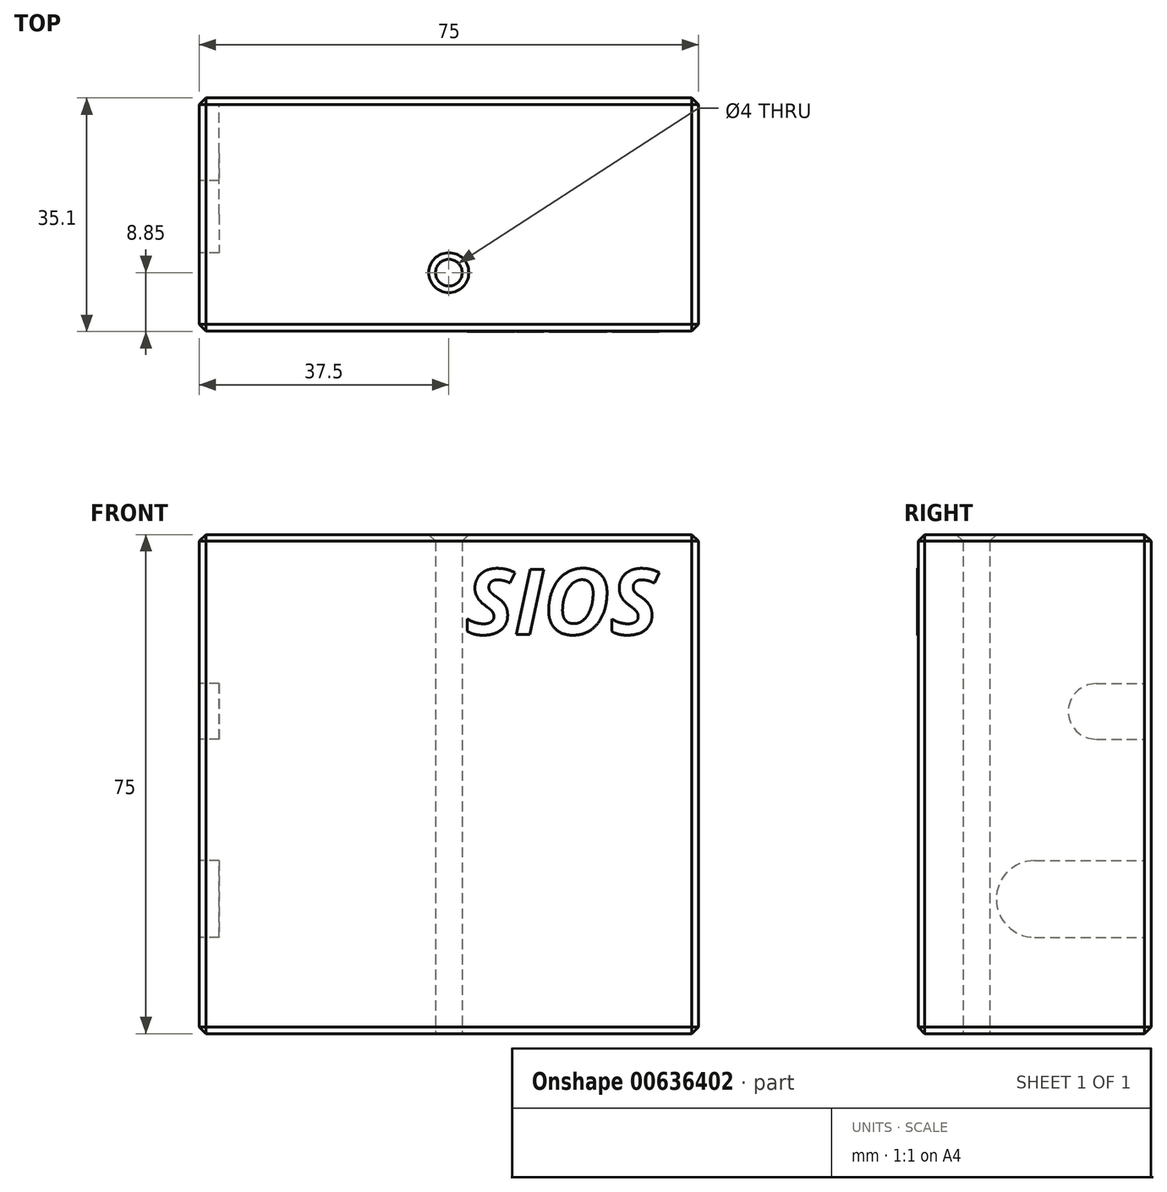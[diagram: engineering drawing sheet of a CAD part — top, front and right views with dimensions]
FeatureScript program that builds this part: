
annotation { "Feature Type Name" : "Feature", "Feature Type Description" : "" }
export const myFeature = defineFeature(function(context is Context, id is Id, definition is map)
    precondition{}
    {
        {
            var Q0;
            Q0=qCreatedBy(makeId("Front.planeOp"),FACE);
            var sketch = newSketch(context, id + "F0", { "sketchPlane" : qUnion([Q0])});
            skLineSegment(sketch, "E0.bottom", {"start": v(-37.5, 37.5) * mm, "end": v(37.5, 37.5) * mm});
            skLineSegment(sketch, "E0.top", {"start": v(-37.5, -37.5) * mm, "end": v(37.5, -37.5) * mm});
            skLineSegment(sketch, "E0.left", {"start": v(-37.5, 37.5) * mm, "end": v(-37.5, -37.5) * mm});
            skLineSegment(sketch, "E0.right", {"start": v(37.5, 37.5) * mm, "end": v(37.5, -37.5) * mm});
            skLineSegment(sketch, "E1", {"start": v(0, 0) * mm, "end": v(0, 37.5) * mm, "construction": true});
            skSolve(sketch);
        }
        {
            var Q0;
            Q0=makeQuery(id+"F0.imprint","IMPRINT",FACE,{"disambiguationData":[TD([[makeQuery(id+"F0.imprint","IMPRINT",EDGE,{"derivedFrom":sQuery(id+"F0.wireOp",EDGE,"E0.bottom")}),-1.0]])]});
            extrude(context, id + "F1", {"entities" : qUnion([Q0]), "endBound" : BoundingType.SYMMETRIC, "depth" : 35 * mm, "offsetDistance" : 25 * mm});
        }
        {
            var Q0;
            Q0=makeQuery(id+"F1.opExtrude","SWEPT_FACE",FACE,{"disambiguationData":[OSD([sQuery(id+"F0.wireOp",EDGE,"E0.top")])]});
            var sketch = newSketch(context, id + "F2", { "sketchPlane" : qUnion([Q0])});
            skPoint(sketch, "E2", {"position": v(0, 8.75) * mm});
            skCircle(sketch, "E3", {"center": v(0, 8.75) * mm, "radius": 2 * mm});
            skSolve(sketch);
        }
        {
            var Q0;
            Q0=makeQuery(id+"F2.imprint","IMPRINT",FACE,{"disambiguationData":[TD([[makeQuery(id+"F2.imprint","IMPRINT",EDGE,{"derivedFrom":sQuery(id+"F2.wireOp",EDGE,"E3")}),1.0]])]});
            var Q1;
            Q1=makeQuery(id+"F1.opExtrude","SWEPT_FACE",FACE,{"disambiguationData":[OSD([sQuery(id+"F0.wireOp",EDGE,"E0.top")])]});
            var Q2;
            Q2=makeQuery(id+"F1.opExtrude","SWEPT_BODY",BODY,{"disambiguationData":[OSD([sQuery(id+"F0.wireOp",EDGE,"E0.bottom"),sQuery(id+"F0.wireOp",EDGE,"E0.top"),sQuery(id+"F0.wireOp",EDGE,"E0.left"),sQuery(id+"F0.wireOp",EDGE,"E0.right")])]});
            extrude(context, id + "F3", {"entities" : qUnion([Q0]), "operationType" : NewBodyOperationType.REMOVE, "endBound" : BoundingType.UP_TO_BODY, "oppositeDirection" : true, "depth" : 25 * mm, "endBoundEntityFace" : qUnion([Q1]), "endBoundEntityBody" : qUnion([Q2]), "offsetDistance" : 25 * mm});
        }
        {
            var Q0;
            Q0=makeQuery(id+"F1.opExtrude","SWEPT_FACE",FACE,{"disambiguationData":[OSD([sQuery(id+"F0.wireOp",EDGE,"E0.bottom")])]});
            var Q1;
            Q1=makeQuery(id+"F1.opExtrude","CAP_FACE",FACE,{"disambiguationData":[OSD([sQuery(id+"F0.wireOp",EDGE,"E0.bottom"),sQuery(id+"F0.wireOp",EDGE,"E0.top"),sQuery(id+"F0.wireOp",EDGE,"E0.left"),sQuery(id+"F0.wireOp",EDGE,"E0.right")])],"isStart":false});
            var Q2;
            Q2=makeQuery(id+"F1.opExtrude","SWEPT_FACE",FACE,{"disambiguationData":[OSD([sQuery(id+"F0.wireOp",EDGE,"E0.left")])]});
            var Q3;
            Q3=makeQuery(id+"F1.opExtrude","CAP_FACE",FACE,{"disambiguationData":[OSD([sQuery(id+"F0.wireOp",EDGE,"E0.bottom"),sQuery(id+"F0.wireOp",EDGE,"E0.top"),sQuery(id+"F0.wireOp",EDGE,"E0.left"),sQuery(id+"F0.wireOp",EDGE,"E0.right")])],"isStart":true});
            var Q4;
            Q4=makeQuery(id+"F1.opExtrude","SWEPT_FACE",FACE,{"disambiguationData":[OSD([sQuery(id+"F0.wireOp",EDGE,"E0.right")])]});
            chamfer(context, id + "F4", {"entities" : qUnion([Q0, Q1, Q2, Q3, Q4]), "width" : 1 * mm, "tangentPropagation" : true});
        }
        {
            var Q0;
            Q0=makeQuery(id+"F1.opExtrude","CAP_FACE",FACE,{"disambiguationData":[OSD([sQuery(id+"F0.wireOp",EDGE,"E0.bottom"),sQuery(id+"F0.wireOp",EDGE,"E0.top"),sQuery(id+"F0.wireOp",EDGE,"E0.left"),sQuery(id+"F0.wireOp",EDGE,"E0.right")])],"isStart":false});
            var sketch = newSketch(context, id + "F5", { "sketchPlane" : qUnion([Q0])});
            skText(sketch, "E4", { "text": "SIOS", "fontName": "OpenSans-BoldItalic.ttf"});
            const initialGuessF5  = {"E4": [0.0025, 0.0225, 1, 0, 0.00987]};
            skSetInitialGuess(sketch, initialGuessF5);
            skSolve(sketch);
        }
        {
            var Q0;
            Q0 = qSketchRegion(id + "F5", true);
            extrude(context, id + "F6", {"entities" : qUnion([Q0]), "operationType" : NewBodyOperationType.ADD, "depth" : 0.1 * mm, "offsetDistance" : 25 * mm});
        }
        {
            var Q0;
            Q0=makeQuery(id+"F1.opExtrude","SWEPT_FACE",FACE,{"disambiguationData":[OSD([sQuery(id+"F0.wireOp",EDGE,"E0.left")])]});
            var sketch = newSketch(context, id + "F7", { "sketchPlane" : qUnion([Q0])});
            skArc(sketch, "E5", {"start": v(0, -23.03) * mm, "mid": v(5.77, -17.26) * mm, "end": v(0, -11.5) * mm});
            skArc(sketch, "E6", {"start": v(-9.24, 6.74) * mm, "mid": v(-5.06, 10.92) * mm, "end": v(-9.24, 15.09) * mm});
            skLineSegment(sketch, "E7", {"start": v(-9.24, 15.09) * mm, "end": v(-16.5, 15.09) * mm});
            skLineSegment(sketch, "E8", {"start": v(-9.24, 6.74) * mm, "end": v(-16.5, 6.74) * mm});
            skLineSegment(sketch, "E9", {"start": v(0, -11.5) * mm, "end": v(-16.5, -11.5) * mm});
            skLineSegment(sketch, "E10", {"start": v(0, -23.03) * mm, "end": v(-16.5, -23.03) * mm});
            skLineSegment(sketch, "E11", {"start": v(-16.5, 15.09) * mm, "end": v(-16.5, 6.74) * mm});
            skLineSegment(sketch, "E12", {"start": v(-16.5, -11.5) * mm, "end": v(-16.5, -23.03) * mm});
            skSolve(sketch);
        }
        {
            var Q0;
            Q0=makeQuery(id+"F7.imprint","IMPRINT",FACE,{"disambiguationData":[TD([[makeQuery(id+"F7.imprint","IMPRINT",EDGE,{"derivedFrom":sQuery(id+"F7.wireOp",EDGE,"E6")}),1.0]])]});
            var Q1;
            Q1=makeQuery(id+"F7.imprint","IMPRINT",FACE,{"disambiguationData":[TD([[makeQuery(id+"F7.imprint","IMPRINT",EDGE,{"derivedFrom":sQuery(id+"F7.wireOp",EDGE,"E5")}),1.0]])]});
            var Q2;
            Q2=makeQuery(id+"F1.opExtrude","SWEPT_BODY",BODY,{"disambiguationData":[OSD([sQuery(id+"F0.wireOp",EDGE,"E0.bottom"),sQuery(id+"F0.wireOp",EDGE,"E0.top"),sQuery(id+"F0.wireOp",EDGE,"E0.left"),sQuery(id+"F0.wireOp",EDGE,"E0.right")])]});
            extrude(context, id + "F8", {"entities" : qUnion([Q0, Q1]), "operationType" : NewBodyOperationType.REMOVE, "oppositeDirection" : true, "depth" : 3 * mm, "endBoundEntityBody" : qUnion([Q2]), "offsetDistance" : 25 * mm});
        }
    });
